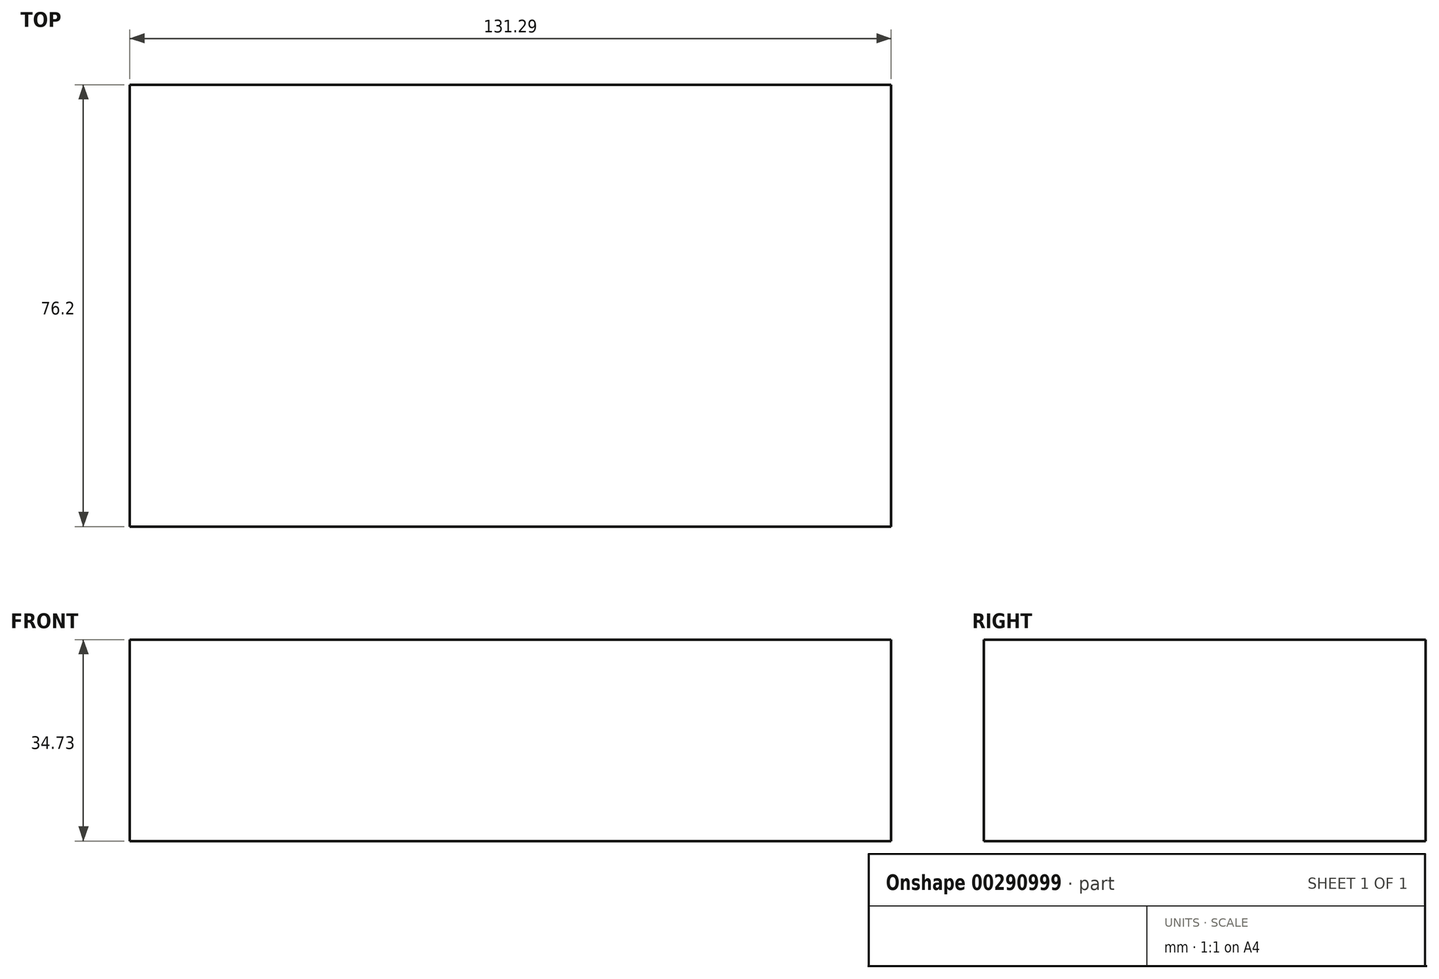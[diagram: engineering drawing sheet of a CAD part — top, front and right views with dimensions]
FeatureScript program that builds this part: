
annotation { "Feature Type Name" : "Feature", "Feature Type Description" : "" }
export const myFeature = defineFeature(function(context is Context, id is Id, definition is map)
    precondition{}
    {
        {
            var Q0;
            Q0=qCreatedBy(makeId("Front.planeOp"),FACE);
            var sketch = newSketch(context, id + "F0", { "sketchPlane" : qUnion([Q0])});
            skLineSegment(sketch, "E0.bottom", {"start": v(-65.5, 17.26) * mm, "end": v(65.78, 17.26) * mm});
            skLineSegment(sketch, "E0.top", {"start": v(-65.5, -17.47) * mm, "end": v(65.78, -17.47) * mm});
            skLineSegment(sketch, "E0.left", {"start": v(-65.5, 17.26) * mm, "end": v(-65.5, -17.47) * mm});
            skLineSegment(sketch, "E0.right", {"start": v(65.78, 17.26) * mm, "end": v(65.78, -17.47) * mm});
            skSolve(sketch);
        }
        {
            var Q0;
            Q0 = qSketchRegion(id + "F0", true);
            extrude(context, id + "F1", {"entities" : qUnion([Q0]), "endBound" : BoundingType.SYMMETRIC, "depth" : 76.2 * mm});
        }
        {
            var Q0;
            Q0=qCreatedBy(makeId("Front.planeOp"),FACE);
            var sketch = newSketch(context, id + "F2", { "sketchPlane" : qUnion([Q0])});
            skLineSegment(sketch, "E1", {"start": v(72.54, -9.3) * mm, "end": v(-67.47, -9.3) * mm});
            skLineSegment(sketch, "E2", {"start": v(72.83, 10.14) * mm, "end": v(-67.47, 10.14) * mm});
            skArc(sketch, "E3", {"start": v(-67.47, 10.14) * mm, "mid": v(-77.2, 0.42) * mm, "end": v(-67.47, -9.3) * mm});
            skSolve(sketch);
        }
        {
            var Q0;
            Q0=sQuery(id+"F2.wireOp",VERTEX,"E2.start");
            var Q1;
            Q1=sQuery(id+"F2.wireOp",EDGE,"E2");
            cPlane(context, id + "F3", {"entities" : qUnion([Q0, Q1]), "cplaneType" : CPlaneType.LINE_POINT, "offset" : 25.4 * mm, "width" : 152.4 * mm, "height" : 152.4 * mm});
        }
        {
            var Q0;
            Q0=qCreatedBy(id+"F3.planeOp",FACE);
            var sketch = newSketch(context, id + "F4", { "sketchPlane" : qUnion([Q0])});
            skCircle(sketch, "E4", {"center": v(0, 10.14) * mm, "radius": 3.8 * mm});
            skSolve(sketch);
        }
    });
